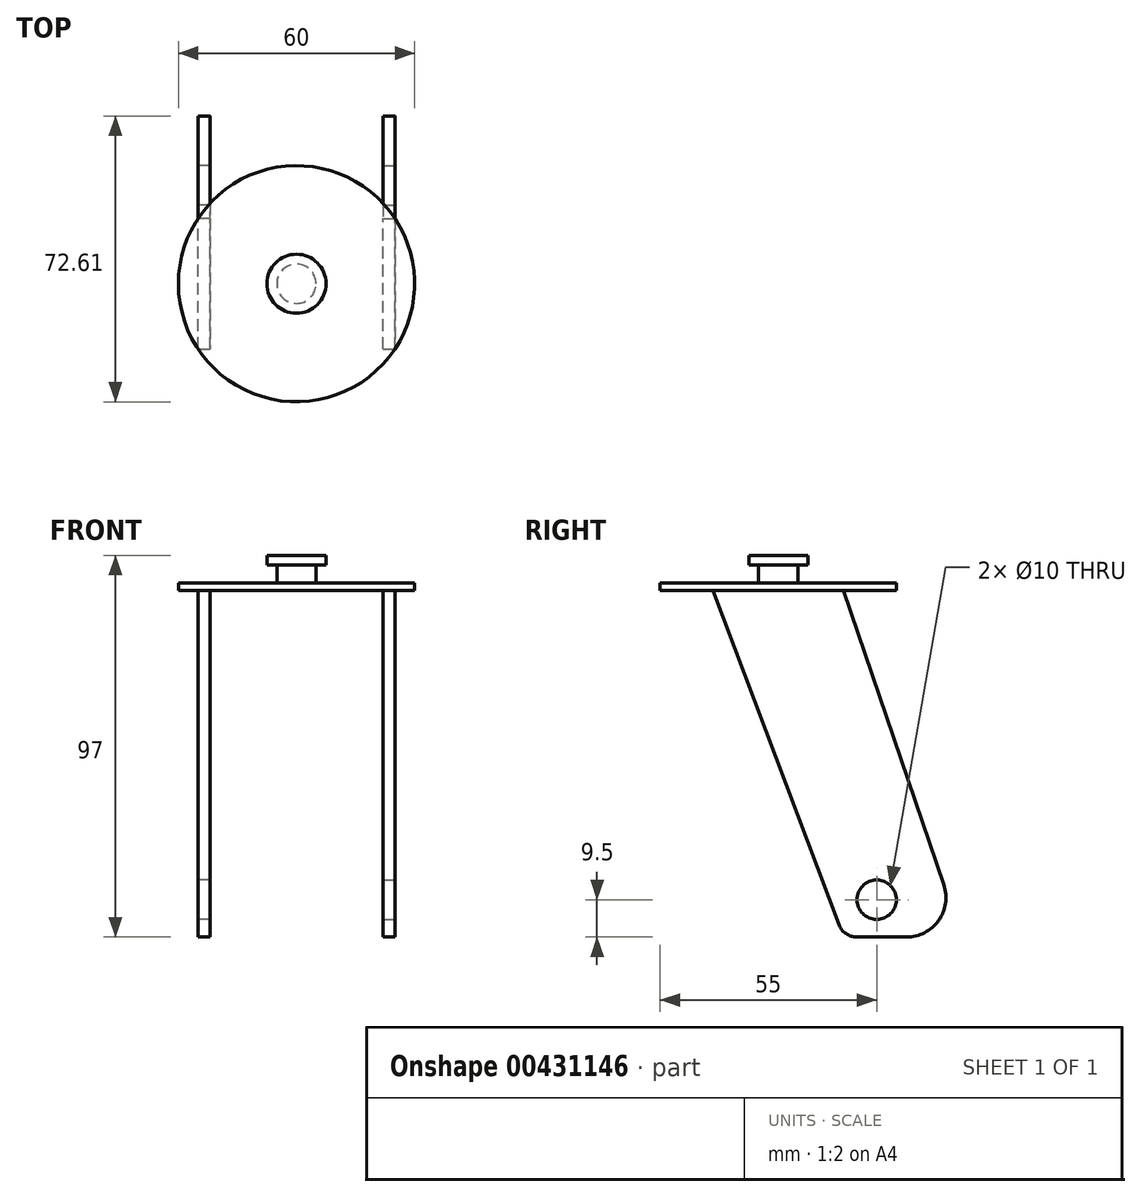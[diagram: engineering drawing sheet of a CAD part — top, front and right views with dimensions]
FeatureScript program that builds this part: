
annotation { "Feature Type Name" : "Feature", "Feature Type Description" : "" }
export const myFeature = defineFeature(function(context is Context, id is Id, definition is map)
    precondition{}
    {
        {
            var Q0;
            Q0=qCreatedBy(makeId("Top.planeOp"),FACE);
            var sketch = newSketch(context, id + "F0", { "sketchPlane" : qUnion([Q0])});
            skCircle(sketch, "E0", {"center": v(0, 0) * mm, "radius": 7.5 * mm});
            skCircle(sketch, "E1", {"center": v(0, 0) * mm, "radius": 5 * mm});
            skSolve(sketch);
        }
        {
            var Q0;
            Q0=makeQuery(id+"F0.imprint","IMPRINT",FACE,{"disambiguationData":[TD([[makeQuery(id+"F0.imprint","IMPRINT",EDGE,{"derivedFrom":sQuery(id+"F0.wireOp",EDGE,"E0")}),1.0]])]});
            extrude(context, id + "F1", {"entities" : qUnion([Q0]), "oppositeDirection" : true, "depth" : 2.5 * mm});
        }
        {
            var Q0;
            Q0=makeQuery(id+"F0.imprint","IMPRINT",FACE,{"disambiguationData":[TD([[makeQuery(id+"F0.imprint","IMPRINT",EDGE,{"derivedFrom":sQuery(id+"F0.wireOp",EDGE,"E1")}),1.0]])]});
            extrude(context, id + "F2", {"entities" : qUnion([Q0]), "operationType" : NewBodyOperationType.ADD, "oppositeDirection" : true, "depth" : 7 * mm});
        }
        {
            var Q0;
            Q0=makeQuery(id+"F2.opExtrude","CAP_FACE",FACE,{"disambiguationData":[OSD([sQuery(id+"F0.wireOp",EDGE,"E1")])],"isStart":false});
            var sketch = newSketch(context, id + "F3", { "sketchPlane" : qUnion([Q0])});
            skPoint(sketch, "E2.middle", {"position": v(0, 0) * mm});
            skCircle(sketch, "E3", {"center": v(0, 0) * mm, "radius": 30 * mm});
            skLineSegment(sketch, "E4", {"start": v(0, 0) * mm, "end": v(-25, 0) * mm, "construction": true});
            skLineSegment(sketch, "E5", {"start": v(0, 0) * mm, "end": v(20, 0) * mm, "construction": true});
            skLineSegment(sketch, "E6", {"start": v(-25, 0) * mm, "end": v(-25, 16.58) * mm});
            skLineSegment(sketch, "E7", {"start": v(-25, 0) * mm, "end": v(-25, -16.58) * mm});
            skLineSegment(sketch, "E8.0", {"start": v(-22, 0) * mm, "end": v(-22, 16.58) * mm});
            skLineSegment(sketch, "E8.1", {"start": v(-22, 0) * mm, "end": v(-22, -16.58) * mm});
            skLineSegment(sketch, "E9", {"start": v(-22, 16.58) * mm, "end": v(-25, 16.58) * mm});
            skLineSegment(sketch, "E10", {"start": v(-22, -16.58) * mm, "end": v(-25, -16.58) * mm});
            skLineSegment(sketch, "E11", {"start": v(0, 30) * mm, "end": v(0, -30) * mm, "construction": true});
            skLineSegment(sketch, "E12.MirrorCS", {"start": v(22, 0) * mm, "end": v(22, 16.58) * mm});
            skLineSegment(sketch, "E13.MirrorCS", {"start": v(25, 0) * mm, "end": v(25, 16.58) * mm});
            skLineSegment(sketch, "E14.MirrorCS", {"start": v(22, 16.58) * mm, "end": v(25, 16.58) * mm});
            skLineSegment(sketch, "E15.MirrorCS", {"start": v(25, 0) * mm, "end": v(25, -16.58) * mm});
            skLineSegment(sketch, "E16.MirrorCS", {"start": v(22, 0) * mm, "end": v(22, -16.58) * mm});
            skLineSegment(sketch, "E17.MirrorCS", {"start": v(22, -16.58) * mm, "end": v(25, -16.58) * mm});
            skSolve(sketch);
        }
        {
            var Q0;
            Q0=makeQuery(id+"F3.imprint","IMPRINT",FACE,{"disambiguationData":[TD([[makeQuery(id+"F3.imprint","IMPRINT",EDGE,{"derivedFrom":sQuery(id+"F3.wireOp",EDGE,"E8.0")}),-1.0]])]});
            var Q1;
            {var subQ0=sQuery(id+"F3.wireOp",EDGE,"E6");Q1=makeQuery(id+"F3.imprint","IMPRINT",FACE,{"disambiguationData":[TD([[makeQuery(id+"F3.imprint","IMPRINT",EDGE,{"derivedFrom":subQ0}),1.0]])]});}
            var Q2;
            {var subQ0=sQuery(id+"F3.wireOp",EDGE,"E13.MirrorCS");Q2=makeQuery(id+"F3.imprint","IMPRINT",FACE,{"disambiguationData":[TD([[makeQuery(id+"F3.imprint","IMPRINT",EDGE,{"derivedFrom":subQ0}),-1.0]])]});}
            var Q3;
            Q3=makeQuery(id+"F3.imprint","IMPRINT",FACE,{"disambiguationData":[TD([[makeQuery(id+"F3.imprint","IMPRINT",EDGE,{"derivedFrom":makeQuery(id+"F2.opExtrude","CAP_EDGE",EDGE,{"disambiguationData":[OSD([sQuery(id+"F0.wireOp",EDGE,"E1")])],"isStart":false})}),-1.0]])]});
            extrude(context, id + "F4", {"entities" : qUnion([Q0, Q1, Q2, Q3]), "operationType" : NewBodyOperationType.ADD, "depth" : 2 * mm});
        }
        {
            var Q0;
            Q0=makeQuery(id+"F3.imprint","IMPRINT",FACE,{"disambiguationData":[TD([[makeQuery(id+"F3.imprint","IMPRINT",EDGE,{"derivedFrom":sQuery(id+"F3.wireOp",EDGE,"E6")}),-1.0]])]});
            var Q1;
            Q1=makeQuery(id+"F3.imprint","IMPRINT",FACE,{"disambiguationData":[TD([[makeQuery(id+"F3.imprint","IMPRINT",EDGE,{"derivedFrom":sQuery(id+"F3.wireOp",EDGE,"E12.MirrorCS")}),-1.0]])]});
            extrude(context, id + "F5", {"entities" : qUnion([Q0, Q1]), "operationType" : NewBodyOperationType.ADD, "depth" : 90 * mm});
        }
        {
            var Q0;
            Q0=makeQuery(id+"F5.opExtrude","SWEPT_FACE",FACE,{"disambiguationData":[OSD([sQuery(id+"F3.wireOp",EDGE,"E13.MirrorCS"),sQuery(id+"F3.wireOp",EDGE,"E15.MirrorCS")])]});
            var sketch = newSketch(context, id + "F6", { "sketchPlane" : qUnion([Q0])});
            skLineSegment(sketch, "E18", {"start": v(0, 0) * mm, "end": v(25, 0) * mm, "construction": true});
            skLineSegment(sketch, "E19", {"start": v(0, 0) * mm, "end": v(0, -87.5) * mm, "construction": true});
            skPoint(sketch, "E19.endSnap0", {"position": v(0, -97) * mm});
            skCircle(sketch, "E20", {"center": v(25, -87.5) * mm, "radius": 5 * mm});
            skLineSegment(sketch, "E21", {"start": v(-16.58, -9) * mm, "end": v(16.58, -97) * mm});
            skLineSegment(sketch, "E22", {"start": v(16.58, -97) * mm, "end": v(46.58, -97) * mm});
            skLineSegment(sketch, "E23", {"start": v(46.58, -97) * mm, "end": v(16.58, -9) * mm});
            skSolve(sketch);
        }
        {
            var Q0;
            Q0=makeQuery(id+"F6.imprint","IMPRINT",FACE,{"disambiguationData":[TD([[makeQuery(id+"F6.imprint","IMPRINT",EDGE,{"derivedFrom":sQuery(id+"F6.wireOp",EDGE,"E21")}),-1.0]])]});
            extrude(context, id + "F7", {"entities" : qUnion([Q0]), "operationType" : NewBodyOperationType.REMOVE, "oppositeDirection" : true, "depth" : 3 * mm});
        }
        {
            var Q0;
            Q0=makeQuery(id+"F6.imprint","IMPRINT",FACE,{"disambiguationData":[TD([[makeQuery(id+"F6.imprint","IMPRINT",EDGE,{"derivedFrom":sQuery(id+"F6.wireOp",EDGE,"E20")}),-1.0]])]});
            extrude(context, id + "F8", {"entities" : qUnion([Q0]), "operationType" : NewBodyOperationType.ADD, "oppositeDirection" : true, "depth" : 3 * mm});
        }
        {
            var Q0;
            Q0=makeQuery(id+"F5.opExtrude","SWEPT_FACE",FACE,{"disambiguationData":[OSD([sQuery(id+"F3.wireOp",EDGE,"E6"),sQuery(id+"F3.wireOp",EDGE,"E7")])]});
            var sketch = newSketch(context, id + "F9", { "sketchPlane" : qUnion([Q0])});
            skLineSegment(sketch, "E24", {"start": v(0, 0) * mm, "end": v(-25, 0) * mm, "construction": true});
            skLineSegment(sketch, "E25", {"start": v(0, 0) * mm, "end": v(0, -87.5) * mm, "construction": true});
            skCircle(sketch, "E26", {"center": v(-25, -87.5) * mm, "radius": 5 * mm});
            skLineSegment(sketch, "E27", {"start": v(16.58, -9) * mm, "end": v(-16.58, -97) * mm});
            skLineSegment(sketch, "E28", {"start": v(-16.58, -97) * mm, "end": v(-46.58, -97) * mm});
            skLineSegment(sketch, "E29", {"start": v(-46.58, -97) * mm, "end": v(-16.58, -9) * mm});
            skSolve(sketch);
        }
        {
            var Q0;
            Q0=makeQuery(id+"F9.imprint","IMPRINT",FACE,{"disambiguationData":[TD([[makeQuery(id+"F9.imprint","IMPRINT",EDGE,{"derivedFrom":sQuery(id+"F9.wireOp",EDGE,"E27")}),1.0]])]});
            extrude(context, id + "F10", {"entities" : qUnion([Q0]), "operationType" : NewBodyOperationType.REMOVE, "oppositeDirection" : true, "depth" : 3 * mm});
        }
        {
            var Q0;
            Q0=makeQuery(id+"F9.imprint","IMPRINT",FACE,{"disambiguationData":[TD([[makeQuery(id+"F9.imprint","IMPRINT",EDGE,{"derivedFrom":sQuery(id+"F9.wireOp",EDGE,"E26")}),-1.0]])]});
            extrude(context, id + "F11", {"entities" : qUnion([Q0]), "operationType" : NewBodyOperationType.ADD, "oppositeDirection" : true, "depth" : 3 * mm});
        }
        {
            var Q0;
            Q0=makeQuery(id+"F11.opExtrude","SWEPT_EDGE",EDGE,{"disambiguationData":[OSD([sQuery(id+"F9.wireOp",EDGE,"E28"),sQuery(id+"F9.wireOp",EDGE,"E29")])]});
            var Q1;
            Q1=makeQuery(id+"F8.opExtrude","SWEPT_EDGE",EDGE,{"disambiguationData":[OSD([sQuery(id+"F6.wireOp",EDGE,"E22"),sQuery(id+"F6.wireOp",EDGE,"E23")])]});
            fillet(context, id + "F12", {"entities" : qUnion([Q0, Q1]), "radius" : 10 * mm, "tangentPropagation" : true, "allowEdgeOverflow" : false});
        }
        {
            var Q0;
            {var subQ0=sQuery(id+"F9.wireOp",EDGE,"E28");var subQ1=sQuery(id+"F9.wireOp",EDGE,"E27");var subQ2=sQuery(id+"F3.wireOp",EDGE,"E10");var subQ3=sQuery(id+"F3.wireOp",EDGE,"E7");var subQ4=sQuery(id+"F3.wireOp",EDGE,"E6");var subQ5=sQuery(id+"F3.wireOp",EDGE,"E3");Q0=makeQuery(id+"F11.boolean.opBoolean","MERGE",EDGE,{"derivedFrom":[makeQuery(id+"F10.boolean.opBoolean","MERGE",EDGE,{"derivedFrom":[makeQuery(id+"F5.opExtrude","CAP_EDGE",EDGE,{"disambiguationData":[OSD([subQ2])],"isStart":false}),makeQuery(id+"F10.opExtrude","SWEPT_EDGE",EDGE,{"disambiguationData":[OSD([subQ5,subQ4,subQ3,subQ2,subQ1,subQ0])]})]}),makeQuery(id+"F11.opExtrude","SWEPT_EDGE",EDGE,{"disambiguationData":[OSD([subQ5,subQ4,subQ3,subQ2,subQ1,subQ0])]})]});}
            fillet(context, id + "F13", {"entities" : qUnion([Q0]), "radius" : 5 * mm, "tangentPropagation" : true, "allowEdgeOverflow" : false});
        }
        {
            var Q0;
            {var subQ0=sQuery(id+"F6.wireOp",EDGE,"E22");var subQ1=sQuery(id+"F6.wireOp",EDGE,"E21");var subQ2=sQuery(id+"F3.wireOp",EDGE,"E17.MirrorCS");var subQ3=sQuery(id+"F3.wireOp",EDGE,"E15.MirrorCS");var subQ4=sQuery(id+"F3.wireOp",EDGE,"E13.MirrorCS");var subQ5=sQuery(id+"F3.wireOp",EDGE,"E3");Q0=makeQuery(id+"F8.boolean.opBoolean","MERGE",EDGE,{"derivedFrom":[makeQuery(id+"F7.boolean.opBoolean","MERGE",EDGE,{"derivedFrom":[makeQuery(id+"F5.opExtrude","CAP_EDGE",EDGE,{"disambiguationData":[OSD([subQ2])],"isStart":false}),makeQuery(id+"F7.opExtrude","SWEPT_EDGE",EDGE,{"disambiguationData":[OSD([subQ5,subQ4,subQ3,subQ2,subQ1,subQ0])]})]}),makeQuery(id+"F8.opExtrude","SWEPT_EDGE",EDGE,{"disambiguationData":[OSD([subQ5,subQ4,subQ3,subQ2,subQ1,subQ0])]})]});}
            fillet(context, id + "F14", {"entities" : qUnion([Q0]), "radius" : 5 * mm, "tangentPropagation" : true, "allowEdgeOverflow" : false});
        }
    });
